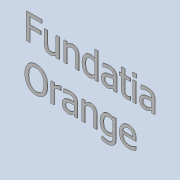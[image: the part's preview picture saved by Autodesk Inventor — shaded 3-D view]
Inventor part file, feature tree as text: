
AUTODESK INVENTOR PART (.ipt)
format: ipt  version: 2020 (Build 240168000, 168)  size: 457,728 bytes
history: native  units: mm
features: extrude x1, sketch x1
ambient origin geometry x8: Origin, YZ Plane, XZ Plane, XY Plane, X Axis, Y Axis, Z Axis, Center Point
bodies: Solid1 (feature_tree)
feature tree (2):
  extrude  "Extrusion1"  Depth=200.0mm
  sketch  "Sketch1"  dims[d0=300.0mm d1=200.0mm d2=0.6mm d3=0.0mm d4=50.0mm d5=50.0mm d6=20.0mm]
